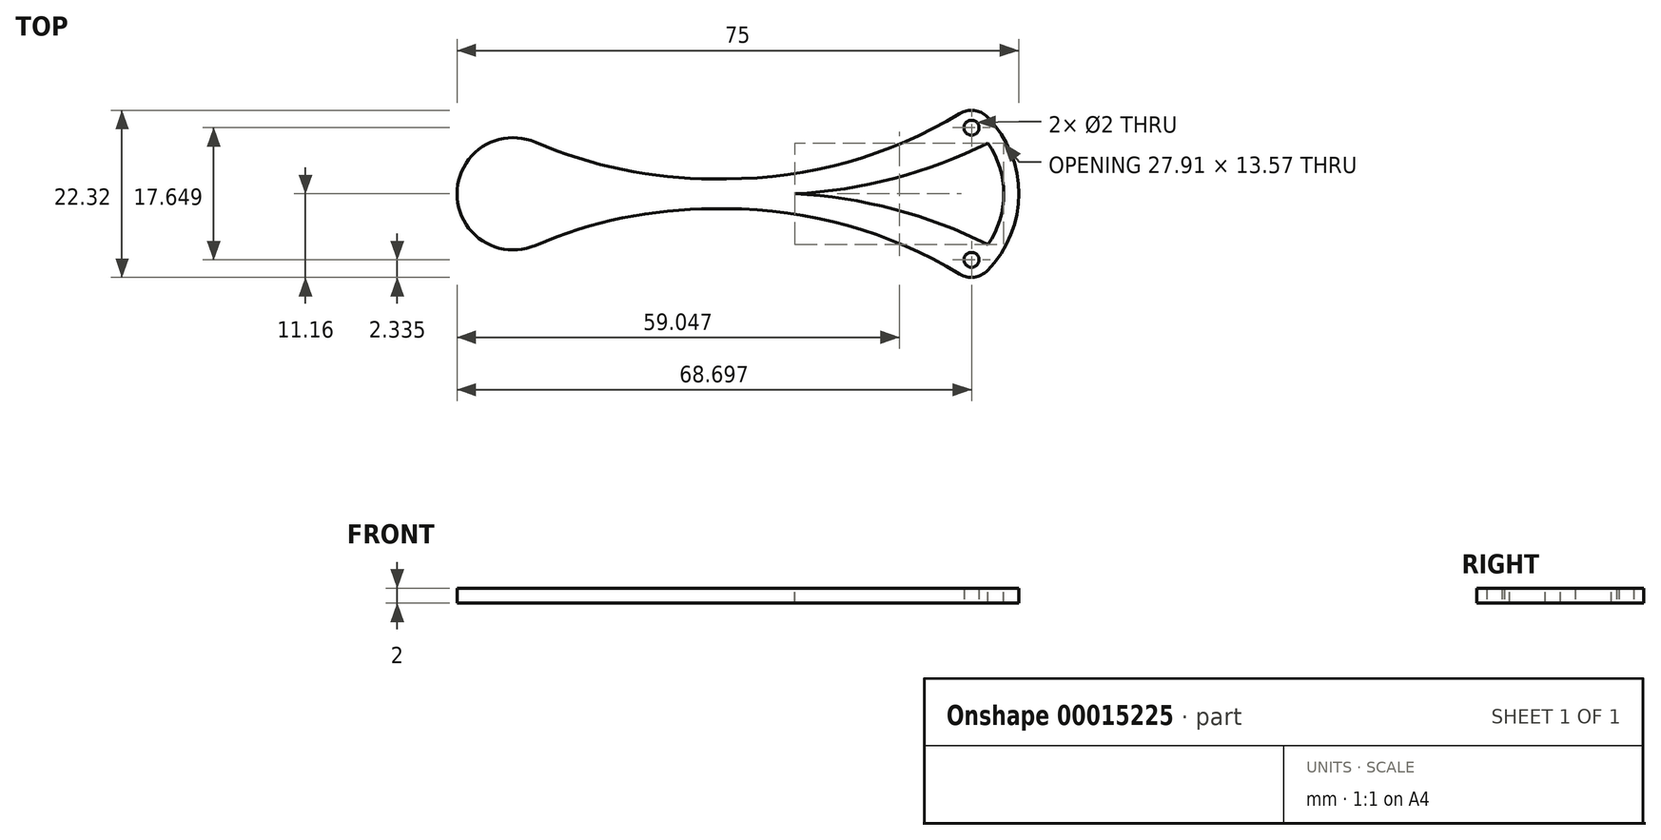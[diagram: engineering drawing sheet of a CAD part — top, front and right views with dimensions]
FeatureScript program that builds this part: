
annotation { "Feature Type Name" : "Feature", "Feature Type Description" : "" }
export const myFeature = defineFeature(function(context is Context, id is Id, definition is map)
    precondition{}
    {
        {
            var Q0;
            Q0=qCreatedBy(makeId("Top.planeOp"),FACE);
            var sketch = newSketch(context, id + "F0", { "sketchPlane" : qUnion([Q0])});
            skCircle(sketch, "E0", {"center": v(-30, 0) * mm, "radius": 7.5 * mm});
            skLineSegment(sketch, "E1", {"start": v(-22.77, 2) * mm, "end": v(18.73, 2) * mm});
            skLineSegment(sketch, "E2", {"start": v(-22.77, -2) * mm, "end": v(18.73, -2) * mm});
            skLineSegment(sketch, "E3", {"start": v(18.73, -2) * mm, "end": v(31.2, -12.03) * mm});
            skLineSegment(sketch, "E4", {"start": v(18.73, 2) * mm, "end": v(31.2, 12.03) * mm});
            skArc(sketch, "E5", {"start": v(31.2, -12.03) * mm, "mid": v(37.5, 0) * mm, "end": v(31.2, 12.03) * mm});
            skCircle(sketch, "E6", {"center": v(31.2, 8.82) * mm, "radius": 1 * mm});
            skLineSegment(sketch, "E7", {"start": v(-37.5, 0) * mm, "end": v(37.5, 0) * mm, "construction": true});
            skCircle(sketch, "E8.MirrorC", {"center": v(31.2, -8.82) * mm, "radius": 1 * mm});
            skSolve(sketch);
        }
        {
            var Q0;
            {var subQ1=sQuery(id+"F0.wireOp",EDGE,"E1");Q0=makeQuery(id+"F0.imprint","IMPRINT",FACE,{"disambiguationData":[TD([[makeQuery(id+"F0.imprint","IMPRINT",EDGE,{"derivedFrom":subQ1}),-1.0]])]});}
            var Q1;
            {var subQ0=sQuery(id+"F0.wireOp",EDGE,"E0");var subQ2=makeQuery(id+"F0.imprint","INTERSECT",VERTEX,{"derivedFrom":[subQ0,sQuery(id+"F0.wireOp",EDGE,"E1")]});Q1=makeQuery(id+"F0.imprint","IMPRINT",FACE,{"disambiguationData":[TD([[makeQuery(id+"F0.imprint","IMPRINT",EDGE,{"disambiguationData":[TD([[subQ2,-1.0]])],"derivedFrom":subQ0}),1.0]])]});}
            extrude(context, id + "F1", {"entities" : qUnion([Q0, Q1]), "depth" : 2 * mm});
        }
        {
            var Q0;
            Q0=makeQuery(id+"F1.opExtrude","SWEPT_EDGE",EDGE,{"disambiguationData":[OSD([sQuery(id+"F0.wireOp",EDGE,"E3"),sQuery(id+"F0.wireOp",EDGE,"E5")])]});
            var Q1;
            Q1=makeQuery(id+"F1.opExtrude","SWEPT_EDGE",EDGE,{"disambiguationData":[OSD([sQuery(id+"F0.wireOp",EDGE,"E4"),sQuery(id+"F0.wireOp",EDGE,"E5")])]});
            fillet(context, id + "F2", {"entities" : qUnion([Q0, Q1]), "radius" : 3 * mm, "tangentPropagation" : true, "allowEdgeOverflow" : false});
        }
        {
            var Q0;
            Q0=makeQuery(id+"F1.opExtrude","SWEPT_EDGE",EDGE,{"disambiguationData":[OSD([sQuery(id+"F0.wireOp",EDGE,"E2"),sQuery(id+"F0.wireOp",EDGE,"E3")])]});
            var Q1;
            Q1=makeQuery(id+"F1.opExtrude","SWEPT_EDGE",EDGE,{"disambiguationData":[OSD([sQuery(id+"F0.wireOp",EDGE,"E1"),sQuery(id+"F0.wireOp",EDGE,"E4")])]});
            var Q2;
            Q2=makeQuery(id+"F1.opExtrude","SWEPT_EDGE",EDGE,{"disambiguationData":[OSD([sQuery(id+"F0.wireOp",EDGE,"E0"),sQuery(id+"F0.wireOp",EDGE,"E2")])]});
            var Q3;
            Q3=makeQuery(id+"F1.opExtrude","SWEPT_EDGE",EDGE,{"disambiguationData":[OSD([sQuery(id+"F0.wireOp",EDGE,"E0"),sQuery(id+"F0.wireOp",EDGE,"E1")])]});
            fillet(context, id + "F3", {"entities" : qUnion([Q0, Q1, Q2, Q3]), "radius" : 60 * mm, "tangentPropagation" : true, "allowEdgeOverflow" : false});
        }
        {
            var Q0;
            Q0=makeQuery(id+"F1.opExtrude","CAP_FACE",FACE,{"disambiguationData":[OSD([sQuery(id+"F0.wireOp",EDGE,"E0"),sQuery(id+"F0.wireOp",EDGE,"E1"),sQuery(id+"F0.wireOp",EDGE,"E2"),sQuery(id+"F0.wireOp",EDGE,"E3"),sQuery(id+"F0.wireOp",EDGE,"E4"),sQuery(id+"F0.wireOp",EDGE,"E5"),sQuery(id+"F0.wireOp",EDGE,"E6"),sQuery(id+"F0.wireOp",EDGE,"E8.MirrorC")])],"isStart":false});
            var sketch = newSketch(context, id + "F4", { "sketchPlane" : qUnion([Q0])});
            skArc(sketch, "E9.0", {"start": v(-1.54, -2) * mm, "mid": v(14.63, -4.22) * mm, "end": v(29.6, -10.72) * mm, "construction": true});
            skArc(sketch, "E9.1", {"start": v(29.6, -10.72) * mm, "mid": v(31.54, -11.13) * mm, "end": v(33.3, -10.26) * mm, "construction": true});
            skArc(sketch, "E9.2", {"start": v(33.3, -10.26) * mm, "mid": v(37.5, 0) * mm, "end": v(33.3, 10.26) * mm, "construction": true});
            skArc(sketch, "E9.3", {"start": v(33.3, 10.26) * mm, "mid": v(31.54, 11.13) * mm, "end": v(29.6, 10.72) * mm, "construction": true});
            skArc(sketch, "E9.4", {"start": v(29.6, 10.72) * mm, "mid": v(14.63, 4.22) * mm, "end": v(-1.54, 2) * mm, "construction": true});
            skLineSegment(sketch, "E10", {"start": v(-1.54, -2) * mm, "end": v(-1.54, 2) * mm, "construction": true});
            skArc(sketch, "E11.0", {"start": v(33.4, -6.78) * mm, "mid": v(35.5, 0) * mm, "end": v(33.4, 6.78) * mm});
            skArc(sketch, "E11.1", {"start": v(7.6, 0) * mm, "mid": v(20.85, -2.05) * mm, "end": v(33.4, -6.78) * mm});
            skArc(sketch, "E11.2", {"start": v(33.4, 6.78) * mm, "mid": v(20.85, 2.05) * mm, "end": v(7.6, 0) * mm});
            skCircle(sketch, "E12.0", {"center": v(31.2, 8.82) * mm, "radius": 1 * mm});
            skCircle(sketch, "E12.1", {"center": v(31.2, -8.82) * mm, "radius": 1 * mm});
            skLineSegment(sketch, "E13", {"start": v(35.5, 0) * mm, "end": v(37.5, 0) * mm});
            skSolve(sketch);
        }
        {
            var Q0;
            Q0=makeQuery(id+"F4.imprint","IMPRINT",FACE,{"disambiguationData":[TD([[makeQuery(id+"F4.imprint","IMPRINT",EDGE,{"derivedFrom":sQuery(id+"F4.wireOp",EDGE,"E11.0")}),1.0]])]});
            extrude(context, id + "F5", {"entities" : qUnion([Q0]), "operationType" : NewBodyOperationType.REMOVE, "endBound" : BoundingType.THROUGH_ALL, "oppositeDirection" : true, "depth" : 25 * mm});
        }
    });
